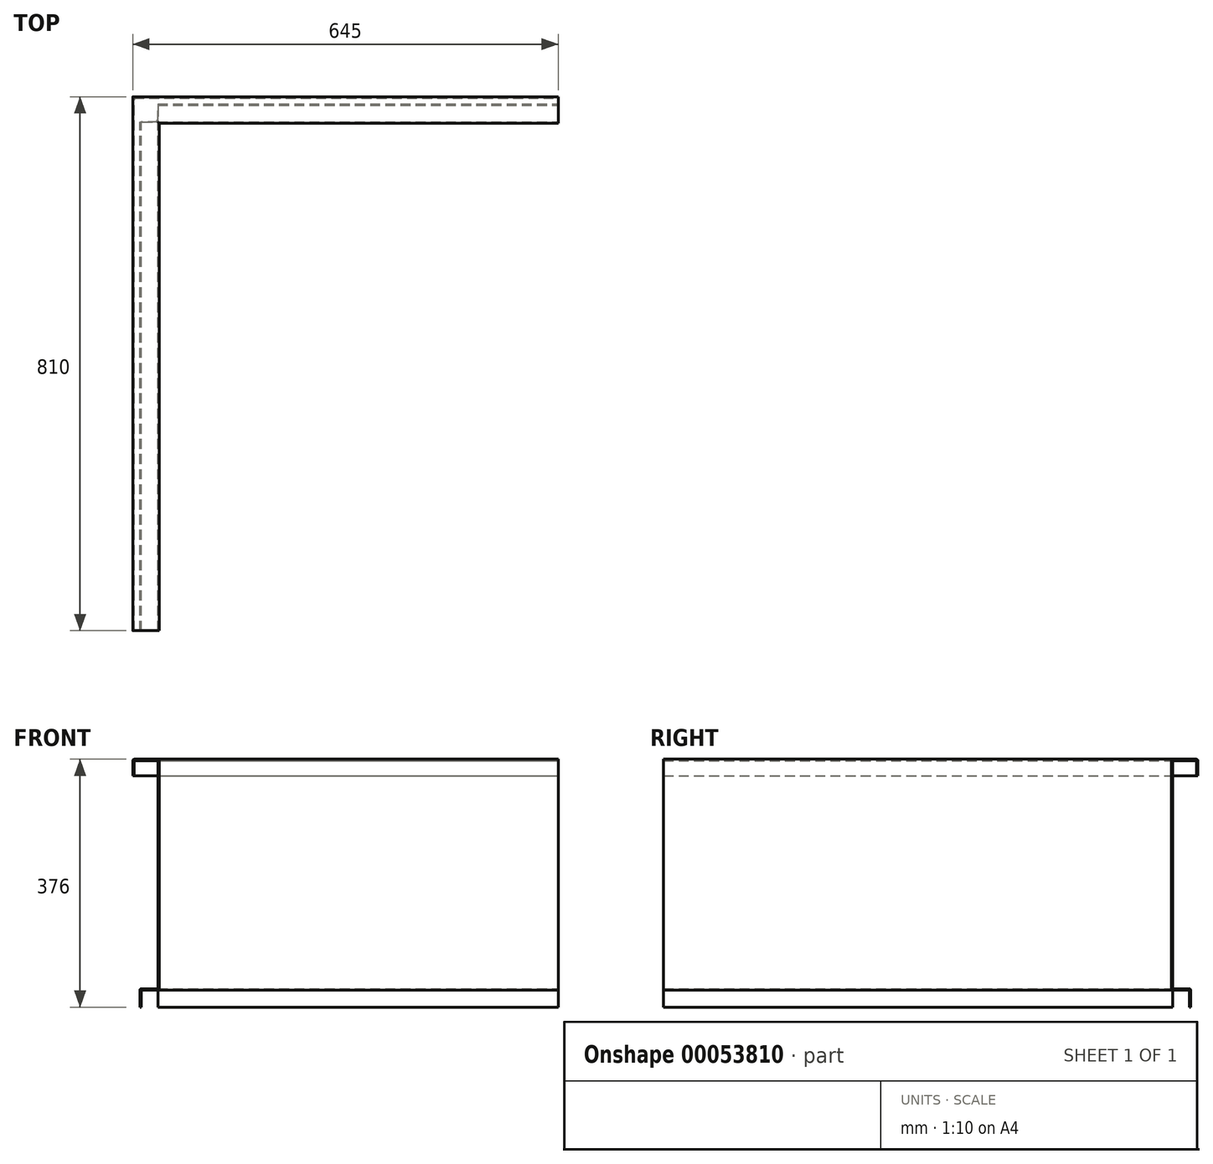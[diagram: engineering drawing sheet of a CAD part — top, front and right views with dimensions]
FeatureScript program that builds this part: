
annotation { "Feature Type Name" : "Feature", "Feature Type Description" : "" }
export const myFeature = defineFeature(function(context is Context, id is Id, definition is map)
    precondition{}
    {
        {
            var Q0;
            Q0=qCreatedBy(makeId("Front.planeOp"),FACE);
            var sketch = newSketch(context, id + "F0", { "sketchPlane" : qUnion([Q0])});
            skLineSegment(sketch, "E0", {"start": v(0, 0) * mm, "end": v(0, -350) * mm});
            skLineSegment(sketch, "E1", {"start": v(0, -350) * mm, "end": v(-27, -350) * mm});
            skLineSegment(sketch, "E2", {"start": v(-27, -350) * mm, "end": v(-27, -376) * mm});
            skLineSegment(sketch, "E3", {"start": v(0, 0) * mm, "end": v(-40, 0) * mm});
            skLineSegment(sketch, "E4", {"start": v(-40, 0) * mm, "end": v(-40, -25) * mm});
            skLineSegment(sketch, "E5.0", {"start": v(-38, -2) * mm, "end": v(-38, -25) * mm});
            skLineSegment(sketch, "E5.1", {"start": v(-29, -348) * mm, "end": v(-29, -376) * mm});
            skLineSegment(sketch, "E5.2", {"start": v(-2, -348) * mm, "end": v(-29, -348) * mm});
            skLineSegment(sketch, "E5.3", {"start": v(-2, -2) * mm, "end": v(-2, -348) * mm});
            skLineSegment(sketch, "E5.4", {"start": v(-2, -2) * mm, "end": v(-38, -2) * mm});
            skLineSegment(sketch, "E6", {"start": v(-40, -25) * mm, "end": v(-38, -25) * mm});
            skLineSegment(sketch, "E7", {"start": v(-29, -376) * mm, "end": v(-27, -376) * mm});
            skSolve(sketch);
        }
        {
            var Q0;
            Q0=qCreatedBy(makeId("Top.planeOp"),FACE);
            var sketch = newSketch(context, id + "F1", { "sketchPlane" : qUnion([Q0])});
            skLineSegment(sketch, "E8", {"start": v(0, 0) * mm, "end": v(0, 770) * mm});
            skLineSegment(sketch, "E9", {"start": v(0, 770) * mm, "end": v(605, 770) * mm});
            skSolve(sketch);
        }
        {
            var Q0;
            Q0=qSketchRegion(id+"F0",true);
            var Q1;
            Q1=qConstructionFilter(qBodyType(qCreatedBy(id+"F1",EDGE),BodyType.WIRE),ConstructionObject.NO);
            sweep(context, id + "F2", {"profiles" : qUnion([Q0]), "path" : qUnion([Q1])});
        }
        {
            var Q0;
            Q0=makeQuery(id+"F2.opSweep","SWEPT_FACE",FACE,{"disambiguationData":[OSD([sQuery(id+"F0.wireOp",EDGE,"E5.2"),sQuery(id+"F1.wireOp",EDGE,"E8")])]});
            var sketch = newSketch(context, id + "F3", { "sketchPlane" : qUnion([Q0])});
            skLineSegment(sketch, "E10.bottom", {"start": v(-2, 772) * mm, "end": v(-29, 772) * mm});
            skLineSegment(sketch, "E10.top", {"start": v(-2, 799) * mm, "end": v(-29, 799) * mm});
            skLineSegment(sketch, "E10.left", {"start": v(-2, 772) * mm, "end": v(-2, 799) * mm});
            skLineSegment(sketch, "E10.right", {"start": v(-29, 772) * mm, "end": v(-29, 799) * mm});
            skSolve(sketch);
        }
        {
            var Q0;
            Q0 = qSketchRegion(id + "F3", true);
            extrude(context, id + "F4", {"entities" : qUnion([Q0]), "operationType" : NewBodyOperationType.REMOVE, "oppositeDirection" : true, "depth" : 30 * mm});
        }
        {
            var Q0;
            Q0=makeQuery(id+"F2.opSweep","SWEPT_EDGE",EDGE,{"disambiguationData":[OSD([sQuery(id+"F0.wireOp",EDGE,"E5.1"),sQuery(id+"F0.wireOp",EDGE,"E5.2"),sQuery(id+"F1.wireOp",EDGE,"E9")])]});
            var Q1;
            Q1=makeQuery(id+"F2.opSweep","SWEPT_EDGE",EDGE,{"disambiguationData":[OSD([sQuery(id+"F0.wireOp",EDGE,"E5.2"),sQuery(id+"F0.wireOp",EDGE,"E5.3"),sQuery(id+"F1.wireOp",EDGE,"E9")])]});
            var Q2;
            Q2=makeQuery(id+"F2.opSweep","SWEPT_EDGE",EDGE,{"disambiguationData":[OSD([sQuery(id+"F0.wireOp",EDGE,"E5.1"),sQuery(id+"F0.wireOp",EDGE,"E5.2"),sQuery(id+"F1.wireOp",EDGE,"E8")])]});
            var Q3;
            Q3=makeQuery(id+"F2.opSweep","SWEPT_EDGE",EDGE,{"disambiguationData":[OSD([sQuery(id+"F0.wireOp",EDGE,"E3"),sQuery(id+"F0.wireOp",EDGE,"E4"),sQuery(id+"F1.wireOp",EDGE,"E8")])]});
            var Q4;
            Q4=makeQuery(id+"F2.opSweep","SWEPT_EDGE",EDGE,{"disambiguationData":[OSD([sQuery(id+"F0.wireOp",EDGE,"E0"),sQuery(id+"F0.wireOp",EDGE,"E3"),sQuery(id+"F1.wireOp",EDGE,"E8")])]});
            var Q5;
            Q5=makeQuery(id+"F2.opSweep","SWEPT_EDGE",EDGE,{"disambiguationData":[OSD([sQuery(id+"F0.wireOp",EDGE,"E0"),sQuery(id+"F0.wireOp",EDGE,"E3"),sQuery(id+"F1.wireOp",EDGE,"E9")])]});
            var Q6;
            Q6=makeQuery(id+"F2.opSweep","SWEPT_EDGE",EDGE,{"disambiguationData":[OSD([sQuery(id+"F0.wireOp",EDGE,"E3"),sQuery(id+"F0.wireOp",EDGE,"E4"),sQuery(id+"F1.wireOp",EDGE,"E9")])]});
            var Q7;
            Q7=makeQuery(id+"F2.opSweep","SWEPT_EDGE",EDGE,{"disambiguationData":[OSD([sQuery(id+"F0.wireOp",EDGE,"E5.3"),sQuery(id+"F0.wireOp",EDGE,"E5.4"),sQuery(id+"F1.wireOp",EDGE,"E9")])]});
            var Q8;
            Q8=makeQuery(id+"F2.opSweep","SWEPT_EDGE",EDGE,{"disambiguationData":[OSD([sQuery(id+"F0.wireOp",EDGE,"E5.0"),sQuery(id+"F0.wireOp",EDGE,"E5.4"),sQuery(id+"F1.wireOp",EDGE,"E9")])]});
            var Q9;
            Q9=makeQuery(id+"F2.opSweep","SWEPT_EDGE",EDGE,{"disambiguationData":[OSD([sQuery(id+"F0.wireOp",EDGE,"E5.3"),sQuery(id+"F0.wireOp",EDGE,"E5.4"),sQuery(id+"F1.wireOp",EDGE,"E8")])]});
            var Q10;
            Q10=makeQuery(id+"F2.opSweep","SWEPT_EDGE",EDGE,{"disambiguationData":[OSD([sQuery(id+"F0.wireOp",EDGE,"E5.0"),sQuery(id+"F0.wireOp",EDGE,"E5.4"),sQuery(id+"F1.wireOp",EDGE,"E8")])]});
            var Q11;
            Q11=makeQuery(id+"F2.opSweep","SWEPT_EDGE",EDGE,{"disambiguationData":[OSD([sQuery(id+"F0.wireOp",EDGE,"E1"),sQuery(id+"F0.wireOp",EDGE,"E2"),sQuery(id+"F1.wireOp",EDGE,"E8")])]});
            var Q12;
            Q12=makeQuery(id+"F2.opSweep","SWEPT_EDGE",EDGE,{"disambiguationData":[OSD([sQuery(id+"F0.wireOp",EDGE,"E0"),sQuery(id+"F0.wireOp",EDGE,"E1"),sQuery(id+"F1.wireOp",EDGE,"E8")])]});
            var Q13;
            Q13=makeQuery(id+"F2.opSweep","SWEPT_EDGE",EDGE,{"disambiguationData":[OSD([sQuery(id+"F0.wireOp",EDGE,"E1"),sQuery(id+"F0.wireOp",EDGE,"E2"),sQuery(id+"F1.wireOp",EDGE,"E9")])]});
            var Q14;
            Q14=makeQuery(id+"F2.opSweep","SWEPT_EDGE",EDGE,{"disambiguationData":[OSD([sQuery(id+"F0.wireOp",EDGE,"E0"),sQuery(id+"F0.wireOp",EDGE,"E1"),sQuery(id+"F1.wireOp",EDGE,"E9")])]});
            fillet(context, id + "F5", {"entities" : qUnion([Q0, Q1, Q2, Q3, Q4, Q5, Q6, Q7, Q8, Q9, Q10, Q11, Q12, Q13, Q14]), "radius" : 2 * mm, "tangentPropagation" : true, "allowEdgeOverflow" : false});
        }
    });
